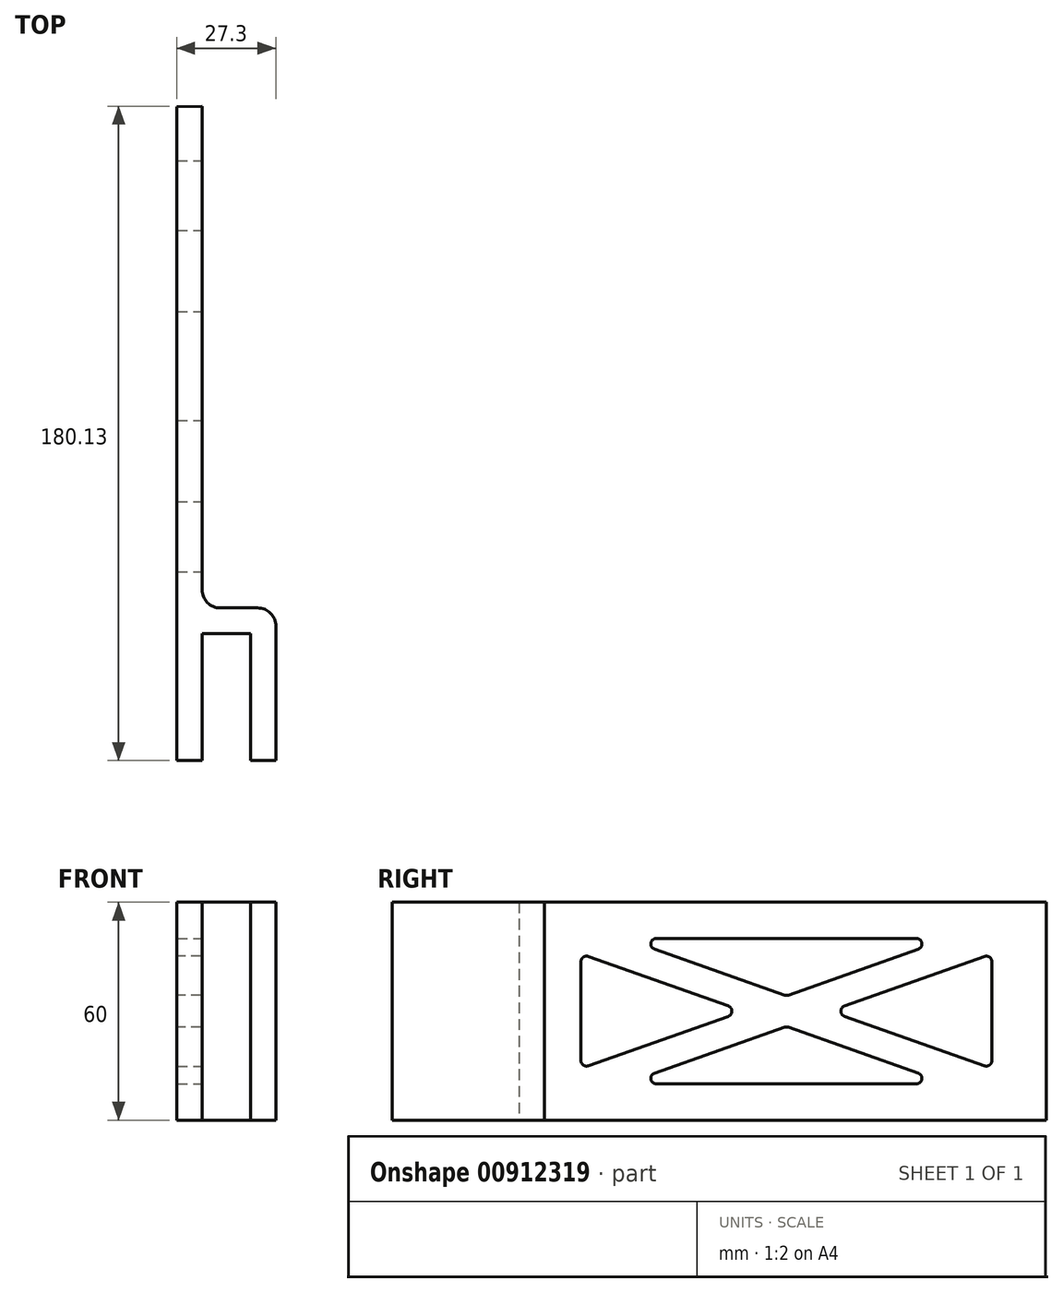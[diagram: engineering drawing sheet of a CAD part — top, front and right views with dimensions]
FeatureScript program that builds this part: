
annotation { "Feature Type Name" : "Feature", "Feature Type Description" : "" }
export const myFeature = defineFeature(function(context is Context, id is Id, definition is map)
    precondition{}
    {
        {
            var Q0;
            Q0=qCreatedBy(makeId("Top.planeOp"),FACE);
            var sketch = newSketch(context, id + "F0", { "sketchPlane" : qUnion([Q0])});
            skLineSegment(sketch, "E0", {"start": v(-27.3, 115.57) * mm, "end": v(-27.3, -64.43) * mm});
            skLineSegment(sketch, "E1", {"start": v(-27.3, -64.43) * mm, "end": v(-20.3, -64.43) * mm});
            skLineSegment(sketch, "E2", {"start": v(-20.3, -64.43) * mm, "end": v(-20.3, -29.43) * mm});
            skLineSegment(sketch, "E3", {"start": v(-20.3, -29.43) * mm, "end": v(-7, -29.43) * mm});
            skLineSegment(sketch, "E4", {"start": v(-7, -29.43) * mm, "end": v(-7, -64.43) * mm});
            skLineSegment(sketch, "E5", {"start": v(-7, -64.43) * mm, "end": v(0, -64.43) * mm});
            skLineSegment(sketch, "E6", {"start": v(0, -64.43) * mm, "end": v(0, -22.43) * mm});
            skLineSegment(sketch, "E7", {"start": v(0, -22.43) * mm, "end": v(-20.3, -22.43) * mm});
            skLineSegment(sketch, "E8", {"start": v(-20.3, -22.43) * mm, "end": v(-20.3, 115.7) * mm});
            skLineSegment(sketch, "E9", {"start": v(-20.3, 115.7) * mm, "end": v(-27.3, 115.57) * mm});
            skSolve(sketch);
        }
        {
            var Q0;
            Q0 = qSketchRegion(id + "F0", true);
            extrude(context, id + "F1", {"entities" : qUnion([Q0]), "depth" : 60 * mm, "offsetDistance" : 25 * mm});
        }
        {
            var Q0;
            Q0=makeQuery(id+"F1.opExtrude","SWEPT_FACE",FACE,{"disambiguationData":[OSD([sQuery(id+"F0.wireOp",EDGE,"E8")])]});
            var sketch = newSketch(context, id + "F2", { "sketchPlane" : qUnion([Q0])});
            skLineSegment(sketch, "E10.bottom", {"start": v(-0.43, 50) * mm, "end": v(88.7, 50) * mm});
            skLineSegment(sketch, "E10.top", {"start": v(-0.43, 10) * mm, "end": v(88.7, 10) * mm});
            skLineSegment(sketch, "E10.left", {"start": v(-12.43, 45.76) * mm, "end": v(-12.43, 14.24) * mm});
            skLineSegment(sketch, "E10.right", {"start": v(100.7, 45.76) * mm, "end": v(100.7, 14.24) * mm});
            skLineSegment(sketch, "E11", {"start": v(-12.43, 14.24) * mm, "end": v(32.13, 30) * mm});
            skLineSegment(sketch, "E12", {"start": v(-0.43, 10) * mm, "end": v(44.13, 25.76) * mm});
            skLineSegment(sketch, "E13", {"start": v(-12.43, 45.76) * mm, "end": v(32.13, 30) * mm});
            skLineSegment(sketch, "E14", {"start": v(-0.43, 50) * mm, "end": v(44.13, 34.24) * mm});
            skLineSegment(sketch, "E15.trimOffspring", {"start": v(44.13, 34.24) * mm, "end": v(88.7, 50) * mm});
            skLineSegment(sketch, "E16.trimOffspring", {"start": v(44.13, 25.76) * mm, "end": v(88.7, 10) * mm});
            skLineSegment(sketch, "E17.trimOffspring", {"start": v(56.13, 30) * mm, "end": v(100.7, 14.24) * mm});
            skLineSegment(sketch, "E18.trimOffspring", {"start": v(56.13, 30) * mm, "end": v(104.55, 47.12) * mm});
            skSolve(sketch);
        }
        {
            var Q0;
            Q0=makeQuery(id+"F2.imprint","IMPRINT",FACE,{"disambiguationData":[TD([[makeQuery(id+"F2.imprint","IMPRINT",EDGE,{"derivedFrom":sQuery(id+"F2.wireOp",EDGE,"E10.left")}),1.0]])]});
            var Q1;
            Q1=makeQuery(id+"F2.imprint","IMPRINT",FACE,{"disambiguationData":[TD([[makeQuery(id+"F2.imprint","IMPRINT",EDGE,{"derivedFrom":sQuery(id+"F2.wireOp",EDGE,"E10.bottom")}),-1.0]])]});
            var Q2;
            {var subQ0=sQuery(id+"F2.wireOp",EDGE,"E10.right");Q2=makeQuery(id+"F2.imprint","IMPRINT",FACE,{"disambiguationData":[TD([[makeQuery(id+"F2.imprint","IMPRINT",EDGE,{"derivedFrom":subQ0}),-1.0]])]});}
            var Q3;
            Q3=makeQuery(id+"F2.imprint","IMPRINT",FACE,{"disambiguationData":[TD([[makeQuery(id+"F2.imprint","IMPRINT",EDGE,{"derivedFrom":sQuery(id+"F2.wireOp",EDGE,"E10.top")}),1.0]])]});
            extrude(context, id + "F3", {"entities" : qUnion([Q0, Q1, Q2, Q3]), "operationType" : NewBodyOperationType.REMOVE, "oppositeDirection" : true, "depth" : 25 * mm, "offsetDistance" : 25 * mm});
        }
        {
            var Q0;
            Q0=makeQuery(id+"F1.opExtrude","SWEPT_EDGE",EDGE,{"disambiguationData":[OSD([sQuery(id+"F0.wireOp",EDGE,"E6"),sQuery(id+"F0.wireOp",EDGE,"E7")])]});
            var Q1;
            Q1=makeQuery(id+"F1.opExtrude","SWEPT_EDGE",EDGE,{"disambiguationData":[OSD([sQuery(id+"F0.wireOp",EDGE,"E7"),sQuery(id+"F0.wireOp",EDGE,"E8")])]});
            fillet(context, id + "F4", {"entities" : qUnion([Q0, Q1]), "radius" : 5 * mm, "tangentPropagation" : true, "allowEdgeOverflow" : false});
        }
        {
            var Q0;
            Q0=makeQuery(id+"F3.boolean.opBoolean","COPY",EDGE,{"derivedFrom":makeQuery(id+"F3.opExtrude","SWEPT_EDGE",EDGE,{"disambiguationData":[OSD([sQuery(id+"F2.wireOp",EDGE,"E10.left"),sQuery(id+"F2.wireOp",EDGE,"E11")])]})});
            var Q1;
            Q1=makeQuery(id+"F3.boolean.opBoolean","COPY",EDGE,{"derivedFrom":makeQuery(id+"F3.opExtrude","SWEPT_EDGE",EDGE,{"disambiguationData":[OSD([sQuery(id+"F2.wireOp",EDGE,"E10.left"),sQuery(id+"F2.wireOp",EDGE,"E13")])]})});
            var Q2;
            Q2=makeQuery(id+"F3.boolean.opBoolean","COPY",EDGE,{"derivedFrom":makeQuery(id+"F3.opExtrude","SWEPT_EDGE",EDGE,{"disambiguationData":[OSD([sQuery(id+"F2.wireOp",EDGE,"E10.top"),sQuery(id+"F2.wireOp",EDGE,"E12")])]})});
            var Q3;
            Q3=makeQuery(id+"F3.boolean.opBoolean","COPY",EDGE,{"derivedFrom":makeQuery(id+"F3.opExtrude","SWEPT_EDGE",EDGE,{"disambiguationData":[OSD([sQuery(id+"F2.wireOp",EDGE,"E10.bottom"),sQuery(id+"F2.wireOp",EDGE,"E14")])]})});
            var Q4;
            Q4=makeQuery(id+"F3.boolean.opBoolean","COPY",EDGE,{"derivedFrom":makeQuery(id+"F3.opExtrude","SWEPT_EDGE",EDGE,{"disambiguationData":[OSD([sQuery(id+"F2.wireOp",EDGE,"E11"),sQuery(id+"F2.wireOp",EDGE,"E13")])]})});
            var Q5;
            Q5=makeQuery(id+"F3.boolean.opBoolean","COPY",EDGE,{"derivedFrom":makeQuery(id+"F3.opExtrude","SWEPT_EDGE",EDGE,{"disambiguationData":[OSD([sQuery(id+"F2.wireOp",EDGE,"E14"),sQuery(id+"F2.wireOp",EDGE,"E15.trimOffspring")])]})});
            var Q6;
            Q6=makeQuery(id+"F3.boolean.opBoolean","COPY",EDGE,{"derivedFrom":makeQuery(id+"F3.opExtrude","SWEPT_EDGE",EDGE,{"disambiguationData":[OSD([sQuery(id+"F2.wireOp",EDGE,"E12"),sQuery(id+"F2.wireOp",EDGE,"E16.trimOffspring")])]})});
            var Q7;
            Q7=makeQuery(id+"F3.boolean.opBoolean","COPY",EDGE,{"derivedFrom":makeQuery(id+"F3.opExtrude","SWEPT_EDGE",EDGE,{"disambiguationData":[OSD([sQuery(id+"F2.wireOp",EDGE,"E17.trimOffspring"),sQuery(id+"F2.wireOp",EDGE,"E18.trimOffspring")])]})});
            var Q8;
            Q8=makeQuery(id+"F3.boolean.opBoolean","COPY",EDGE,{"derivedFrom":makeQuery(id+"F3.opExtrude","SWEPT_EDGE",EDGE,{"disambiguationData":[OSD([sQuery(id+"F2.wireOp",EDGE,"E10.bottom"),sQuery(id+"F2.wireOp",EDGE,"E15.trimOffspring")])]})});
            var Q9;
            Q9=makeQuery(id+"F3.boolean.opBoolean","COPY",EDGE,{"derivedFrom":makeQuery(id+"F3.opExtrude","SWEPT_EDGE",EDGE,{"disambiguationData":[OSD([sQuery(id+"F2.wireOp",EDGE,"E10.right"),sQuery(id+"F2.wireOp",EDGE,"E18.trimOffspring")])]})});
            var Q10;
            Q10=makeQuery(id+"F3.boolean.opBoolean","COPY",EDGE,{"derivedFrom":makeQuery(id+"F3.opExtrude","SWEPT_EDGE",EDGE,{"disambiguationData":[OSD([sQuery(id+"F2.wireOp",EDGE,"E10.right"),sQuery(id+"F2.wireOp",EDGE,"E17.trimOffspring")])]})});
            var Q11;
            Q11=makeQuery(id+"F3.boolean.opBoolean","COPY",EDGE,{"derivedFrom":makeQuery(id+"F3.opExtrude","SWEPT_EDGE",EDGE,{"disambiguationData":[OSD([sQuery(id+"F2.wireOp",EDGE,"E10.top"),sQuery(id+"F2.wireOp",EDGE,"E16.trimOffspring")])]})});
            fillet(context, id + "F5", {"entities" : qUnion([Q0, Q1, Q2, Q3, Q4, Q5, Q6, Q7, Q8, Q9, Q10, Q11]), "radius" : 1.5 * mm, "tangentPropagation" : true, "allowEdgeOverflow" : false});
        }
    });
